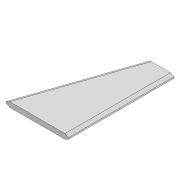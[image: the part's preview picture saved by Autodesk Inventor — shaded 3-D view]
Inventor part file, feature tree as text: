
AUTODESK INVENTOR PART (.ipt)
format: ipt  version: 2022 (Build 260153000, 153)  size: 103,936 bytes
history: native  units: mm
features: chamfer x4, extrude x2, sketch x2, plane x1, projected_geometry x1
ambient origin geometry x8: Origin, YZ Plane, XZ Plane, XY Plane, X Axis, Y Axis, Z Axis, Center Point
bodies: Solid1 (feature_tree)
feature tree (10):
  extrude  "Extrusion1"  Depth=355.0mm
  extrude  "Extrusion2"  Depth=28.0mm TaperAngle=0.0deg
  plane  "Work Plane1"
  chamfer  "Chamfer1"  Distance=150.0mm
  chamfer  "Chamfer2"  [1 undecoded]
  chamfer  "Chamfer3"  Distance=20.0mm Angle=45.0deg
  chamfer  "Chamfer4"  Distance=10.0mm Angle=45.0deg
  sketch  "Sketch1"  dims[d0=600.0mm d1=355.0mm]
  sketch  "Sketch2"  dims[d2=28.0mm d3=0.0mm d5=200.0mm d6=0.0mm d7=150.0mm d8=0.0mm d23=20.0mm d24=10.0mm d25=45.0deg d26=10.0mm d27=20.0mm d28=45.0deg d29=20.0mm d30=10.0mm d31=45.0deg d32=20.0mm d33=10.0mm d34=45.0deg]
  projected_geometry  "Projected Loop1"
note: 1 required parameter value undecoded (feature->parameter linkage not recoverable at this tier; creation-order binding heuristic only, values carry confidence <= 0.55)
